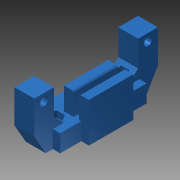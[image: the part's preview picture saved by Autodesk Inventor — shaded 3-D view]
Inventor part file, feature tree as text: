
AUTODESK INVENTOR PART (.ipt)
format: ipt  version: 2013 (Build 170138000, 138)  size: 195,072 bytes
history: native  units: mm
features: extrude x5, sketch x4, chamfer x3, fillet x1
ambient origin geometry x8: Origin, YZ Plane, XZ Plane, XY Plane, X Axis, Y Axis, Z Axis, Center Point
bodies: Solid1 (feature_tree)
feature tree (13):
  extrude  "Extrusion1"  Depth=50.0mm
  extrude  "Extrusion2"  Depth=3.2mm
  extrude  "Extrusion3"  Depth=8.0mm
  extrude  "Extrusion4"  Depth=14.4mm TaperAngle=0.0deg
  extrude  "Extrusion5"  Depth=3.2mm
  chamfer  "Chamfer1"  Distance=3.2mm
  chamfer  "Chamfer2"  Distance=3.0mm
  chamfer  "Chamfer3"  Distance=15.0mm
  fillet  "Fillet2"  Radius=6.1mm
  sketch  "Sketch2"  dims[d0=8.0mm d1=50.0mm]
  sketch  "Sketch3"  dims[d2=3.2mm d3=3.2mm]
  sketch  "Sketch4"  dims[d6=7.0mm d7=0.0mm d8=8.0mm]
  sketch  "Sketch5"  dims[d10=8.0mm d11=14.4mm d12=0.0mm d13=3.2mm d14=3.2mm d15=3.0mm d16=15.0mm d17=0.0mm d18=6.1mm d19=18.0mm d21=4.0mm d23=9.0mm d24=0.0mm d26=4.0mm d27=2.1mm d28=4.0mm d29=4.0mm d30=3.0mm d31=35.0mm d32=3.0mm d33=35.0mm d34=5.6mm d35=5.6mm d36=2.5mm d37=0.0mm d38=4.0mm d39=2.0mm d40=45.0deg d41=8.0mm d42=2.0mm d43=30.0deg d44=8.0mm d45=2.0mm d46=30.0deg d47=1.0mm]
